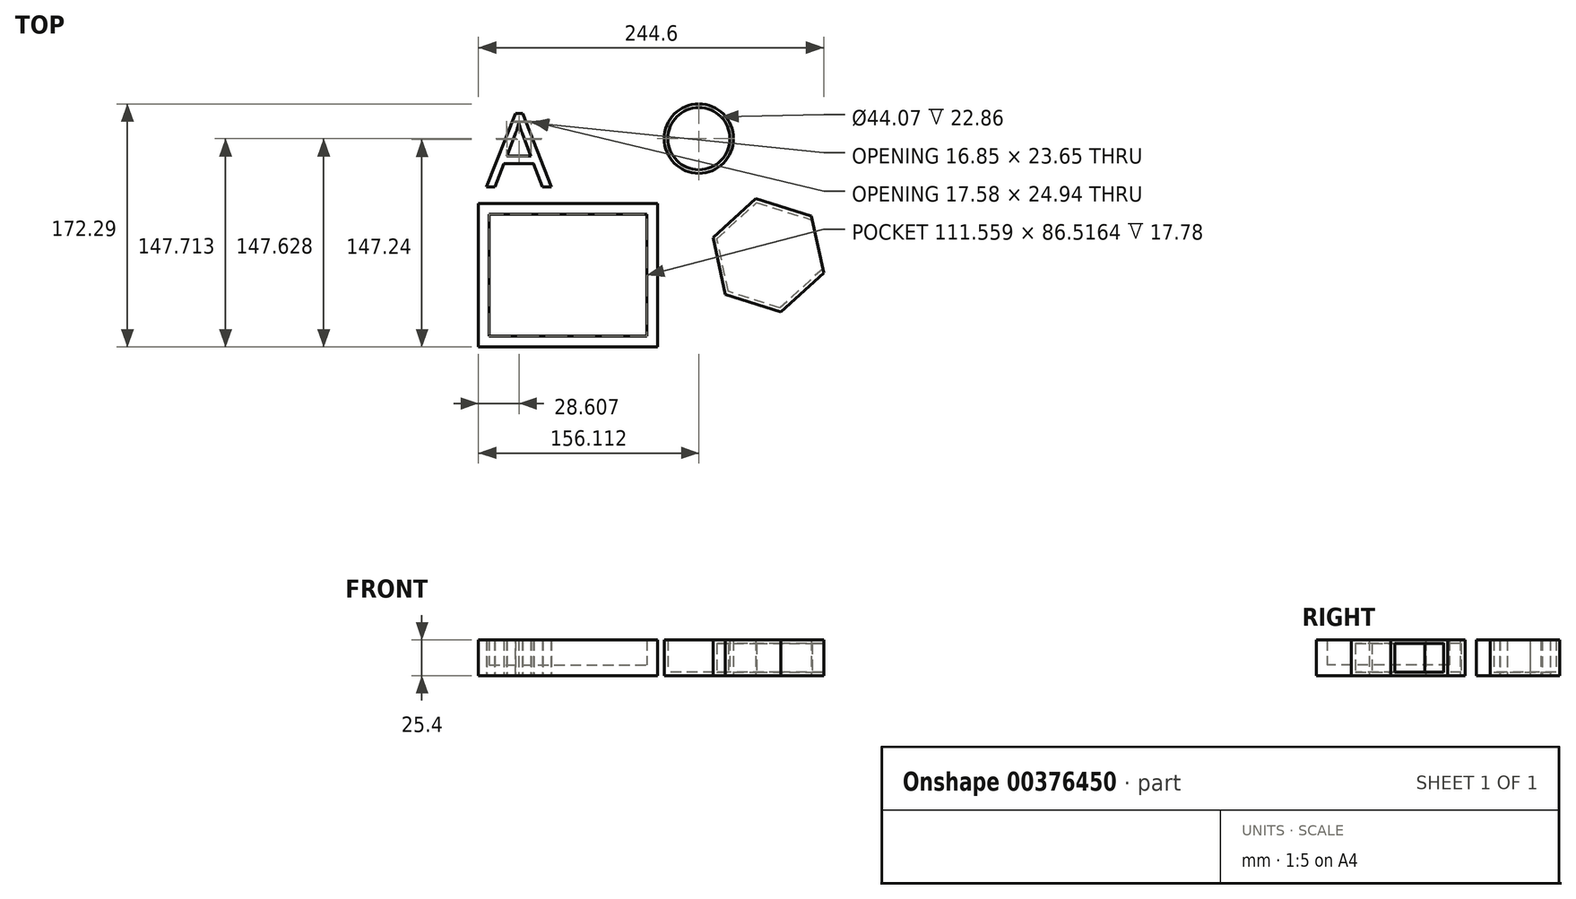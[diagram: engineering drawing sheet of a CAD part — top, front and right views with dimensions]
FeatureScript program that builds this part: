
annotation { "Feature Type Name" : "Feature", "Feature Type Description" : "" }
export const myFeature = defineFeature(function(context is Context, id is Id, definition is map)
    precondition{}
    {
        {
            var Q0;
            Q0=qCreatedBy(makeId("Top.planeOp"),FACE);
            var sketch = newSketch(context, id + "F0", { "sketchPlane" : qUnion([Q0])});
            skLineSegment(sketch, "E0.bottom", {"start": v(-115.85, 0) * mm, "end": v(10.95, 0) * mm});
            skLineSegment(sketch, "E0.top", {"start": v(-115.85, -101.76) * mm, "end": v(10.95, -101.76) * mm});
            skLineSegment(sketch, "E0.left", {"start": v(-115.85, 0) * mm, "end": v(-115.85, -101.76) * mm});
            skLineSegment(sketch, "E0.right", {"start": v(10.95, 0) * mm, "end": v(10.95, -101.76) * mm});
            skCircle(sketch, "E1", {"center": v(40.26, 45.95) * mm, "radius": 24.57 * mm});
            skCircle(sketch, "E2.cCircle", {"center": v(89.5, -36.62) * mm, "radius": 35.67 * mm, "construction": true});
            skLineSegment(sketch, "E2.0", {"start": v(128.75, -49.1) * mm, "end": v(98.31, -76.86) * mm});
            skLineSegment(sketch, "E2.1", {"start": v(98.31, -76.86) * mm, "end": v(59.06, -64.37) * mm});
            skLineSegment(sketch, "E2.2", {"start": v(59.06, -64.37) * mm, "end": v(50.24, -24.14) * mm});
            skLineSegment(sketch, "E2.3", {"start": v(50.24, -24.14) * mm, "end": v(80.68, 3.62) * mm});
            skLineSegment(sketch, "E2.4", {"start": v(80.68, 3.62) * mm, "end": v(119.93, -8.87) * mm});
            skLineSegment(sketch, "E2.5", {"start": v(119.93, -8.87) * mm, "end": v(128.75, -49.1) * mm});
            skPoint(sketch, "E2.0.midPoint", {"position": v(113.53, -62.98) * mm});
            skText(sketch, "E3", { "text": "A", "fontName": "OpenSans-Regular.ttf"});
            const initialGuessF0  = {"E3": [-0.11035, 0.01164, 1, 0, 0.05253]};
            skSetInitialGuess(sketch, initialGuessF0);
            skSolve(sketch);
        }
        {
            var Q0;
            Q0 = qSketchRegion(id + "F0", true);
            extrude(context, id + "F1", {"entities" : qUnion([Q0]), "depth" : 25.4 * mm});
        }
        {
            var Q0;
            Q0=makeQuery(id+"F1.opExtrude","CAP_FACE",FACE,{"disambiguationData":[OSD([sQuery(id+"F0.wireOp",EDGE,"E0.bottom"),sQuery(id+"F0.wireOp",EDGE,"E0.top"),sQuery(id+"F0.wireOp",EDGE,"E0.left"),sQuery(id+"F0.wireOp",EDGE,"E0.right")])],"isStart":false});
            shell(context, id + "F2", {"entities" : qUnion([Q0]), "thickness" : 7.62 * mm});
        }
        {
            var Q0;
            Q0=makeQuery(id+"F1.opExtrude","CAP_FACE",FACE,{"disambiguationData":[OSD([sQuery(id+"F0.wireOp",EDGE,"E1")])],"isStart":false});
            shell(context, id + "F3", {"entities" : qUnion([Q0]), "thickness" : 2.54 * mm});
        }
        {
            var Q0;
            Q0=makeQuery(id+"F1.opExtrude","SWEPT_FACE",FACE,{"disambiguationData":[OSD([sQuery(id+"F0.wireOp",EDGE,"E2.5")])]});
            shell(context, id + "F4", {"entities" : qUnion([Q0]), "thickness" : 2.54 * mm});
        }
        {
            var Q0;
            Q0=makeQuery(id+"F1.opExtrude","SWEPT_FACE",FACE,{"disambiguationData":[OSD([sQuery(id+"F0.wireOp",EDGE,"E3.sketch_text.stroke-5")])]});
            shell(context, id + "F5", {"entities" : qUnion([Q0]), "thickness" : 0.25 * mm});
        }
    });
